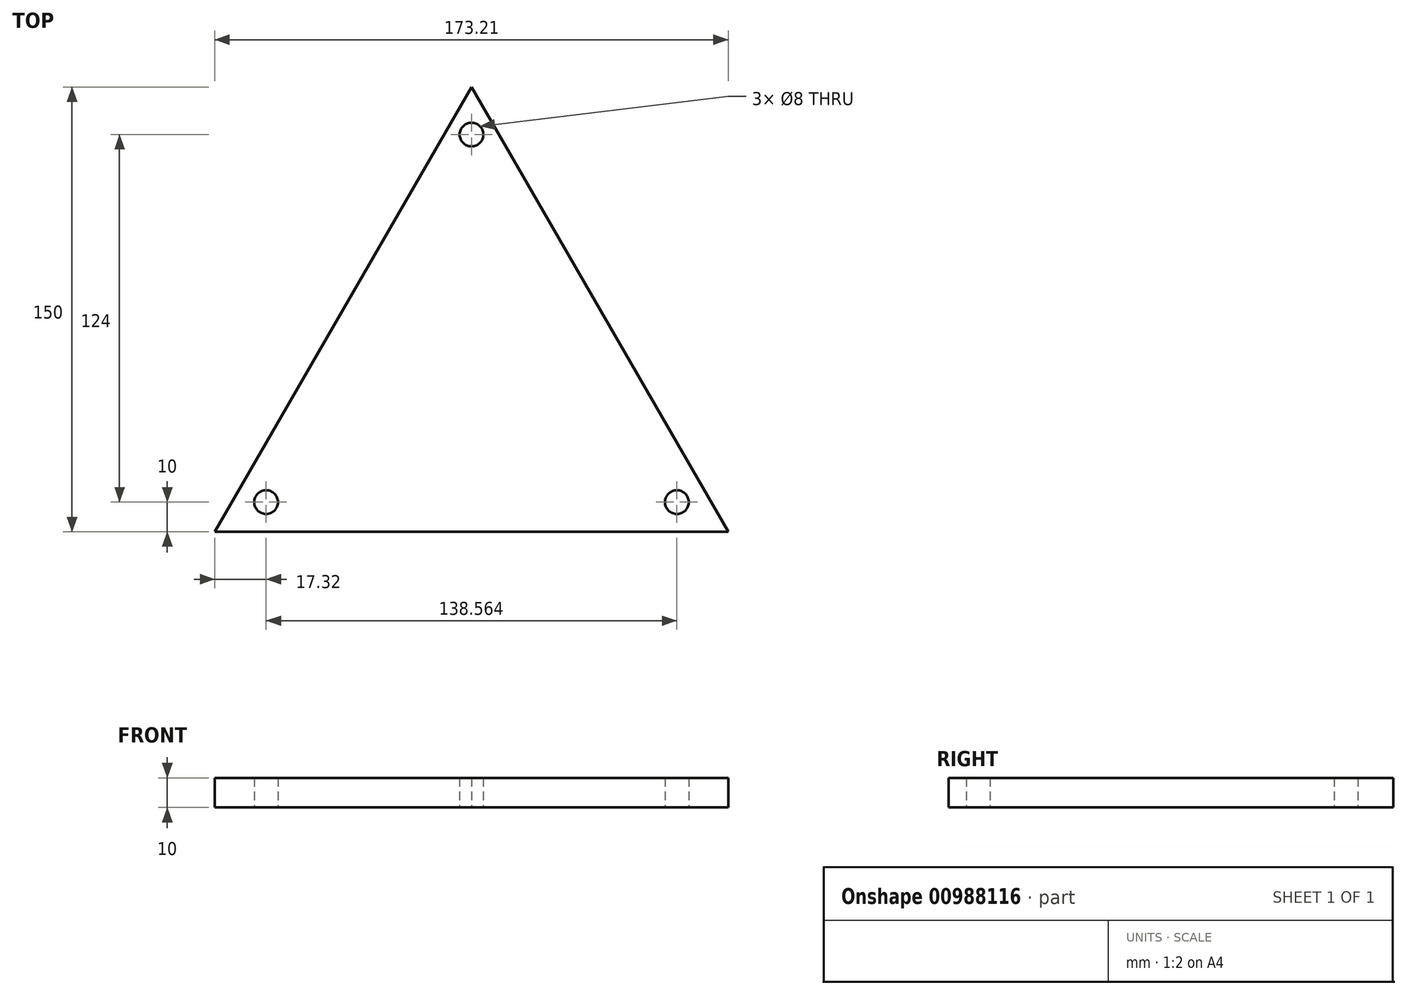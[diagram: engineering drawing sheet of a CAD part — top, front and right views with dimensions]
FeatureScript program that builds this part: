
annotation { "Feature Type Name" : "Feature", "Feature Type Description" : "" }
export const myFeature = defineFeature(function(context is Context, id is Id, definition is map)
    precondition{}
    {
        {
            var Q0;
            Q0=qCreatedBy(makeId("Top.planeOp"),FACE);
            var sketch = newSketch(context, id + "F0", { "sketchPlane" : qUnion([Q0])});
            skLineSegment(sketch, "E0", {"start": v(0, 0) * mm, "end": v(86.6, 150) * mm});
            skLineSegment(sketch, "E1", {"start": v(86.6, 150) * mm, "end": v(173.2, 0) * mm});
            skLineSegment(sketch, "E2", {"start": v(173.2, 0) * mm, "end": v(0, 0) * mm});
            skLineSegment(sketch, "E3", {"start": v(86.6, 150) * mm, "end": v(86.6, 0) * mm, "construction": true});
            skCircle(sketch, "E4", {"center": v(86.6, 134) * mm, "radius": 4 * mm});
            skLineSegment(sketch, "E5", {"start": v(0, 0) * mm, "end": v(129.9, 75) * mm, "construction": true});
            skLineSegment(sketch, "E6", {"start": v(129.9, 75) * mm, "end": v(173.2, 0) * mm, "construction": true});
            skLineSegment(sketch, "E7", {"start": v(173.2, 0) * mm, "end": v(43.3, 75) * mm, "construction": true});
            skCircle(sketch, "E8", {"center": v(17.32, 10) * mm, "radius": 4 * mm});
            skCircle(sketch, "E9", {"center": v(155.88, 10) * mm, "radius": 4 * mm});
            skSolve(sketch);
        }
        {
            var Q0;
            Q0 = qSketchRegion(id + "F0", true);
            extrude(context, id + "F1", {"entities" : qUnion([Q0]), "depth" : 10 * mm, "offsetDistance" : 25 * mm});
        }
    });
